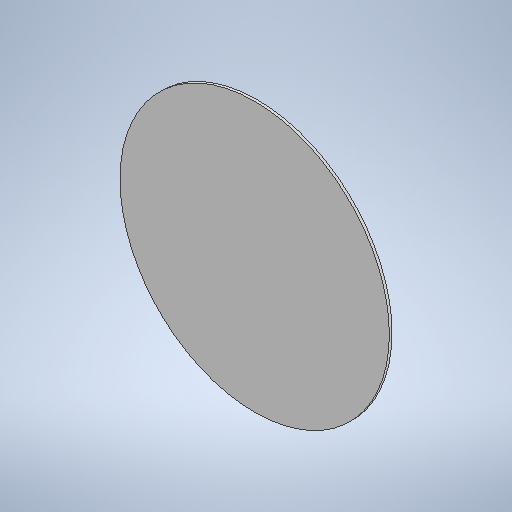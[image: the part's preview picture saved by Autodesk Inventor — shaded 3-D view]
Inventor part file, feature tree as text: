
AUTODESK INVENTOR PART (.ipt)
format: ipt  version: 2025 (Build 290162010, 162A)  size: 222,720 bytes
history: native  units: mm
features: extrude x1, sketch x1
ambient origin geometry x8: Origin, YZ Plane, XZ Plane, XY Plane, X Axis, Y Axis, Z Axis, Center Point
bodies: Solid1 (feature_tree)
feature tree (2):
  extrude  "Extrusion1"  Depth=10.0mm TaperAngle=0.0deg
  sketch  "Sketch1"  dims[d0=1020.0mm d1=10.0mm d2=0.0mm]
